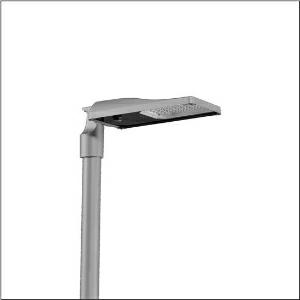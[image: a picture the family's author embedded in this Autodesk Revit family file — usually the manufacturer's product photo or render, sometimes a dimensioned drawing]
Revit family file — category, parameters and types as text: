
# Revit family: streetlight_sl_31_mini___st1_0a_5xh6d31r08ha_6f87
name_source: partatom
category: Lighting Fixtures
units: mm (PartAtom-declared; Revit-internal decimal feet)

## family parameters
Cut with Voids When Loaded = No
Host = Face
Light Source = No
Part Type = Normal
Room Calculation Point = No
Round Connector Dimension = Use Diameter
Shared = No

## types (1)
- --- (1 x LED, 9230 lm, 68.3 W, 3000K)
    Apparent Load = 68 VA
    CIE Flux Codes = 37 72 97 100 100
    Color Rendering = 70
    Color Temperature = 3000K
    Default Elevation = 1800 mm
    Description = Streetlight SL 31 mini D4i, Desk-Remote mast luminaire for post-top, side-entry; light control with lens of PMMA; light distribution: ST1.0a, direct asymmetric distribution, for standard-compliant lighting for roads and squares; LED: luminous flux: 9.230lm, light colour: 730, colour temperature: 3000K; luminous efficacy: 135,1lm/W; control: pre-setting: logarithmic dimming characteristic, flexible luminous flux parameterisation, time-dependent luminous flux control, constant luminous flux control, power reduction, intelligent temperature release in ECG and LED module, overheat protection; luminaire housing, of diecast aluminium, Siteco® metallic grey (DB 702S), corrosivity category C5 high according to DIN EN ISO 12944; cover of toughened safety glass, transparent, opened without tools; mast flange of diecast aluminium, Siteco® metallic grey (DB 702S), spigot size: 76/60mm, mast flange included unmounted; with cable H07RN-F 2x 1.5mm², cable length: 8,5m, connection cable pre-assembled; mains connection: 220..240V, AC, 50/60Hz; power consumption (at start of service life): 68,3W / (at end of service life): 74,5W / (with reduced operation 50%): 29,5W; protection rating (complete): IP66; insulation class (complete): insulation class II (safety insulation); impact resistance: IK09; certification: CE, ENEC, ENEC+, VDE, UKCA, ZD4i; permissible operating ambient temperature for outdoor applications: -40..+50°C; packaging unit: 1 piece

Light Distribution: ST1.0a
    Height = 76 mm
    Lamp = 1 x LED
    Lamp Light Flux = 9230 lm
    Lamp Power = 68.3 W
    Lamp count = 1
    Length = 547 mm
    Luminous efficacy = 135 lm/W
    Manufacturer = Siteco
    ModVariant = No
    Model = 5XH6D31R08HA
    Number of Poles = 1
    OnlyDefault = Yes
    Power Factor = 1
    Product Name = Streetlight SL 31 mini | ST1.0a
    Product group = mast luminaire | pylon top
    ProductGroupID = 6100
    Protection Class = Protection class II
    Protection Degree = IP 66
    RLX_Detail_Level = 1
    RLX_Emergency_Light_Flux = 0 lm
    RLX_Emergency_Type = 0
    RLX_Emergency_Type_DB = No
    RlxData = <blob elided: 24217 chars, md5=82cd78a6>
    Socket = socket
    Standby Power = 0 W
    System Light Flux = 9230 lm
    System Power = 68 W
    Type Comments = factory setting: luminous flux: 100 % | dim-lin: 254 | 692 mA
    Type Image = l_1300328.jpg
    URL = http://relux.com
    VarID = @adj_019341
    Voltage = 0 V
    Weight = 0.00 kg
    Width = 265 mm

## geometry (parser evidence)
native form markers: Blend x4, Sweep x11
no freeform markers — native parametric forms only
